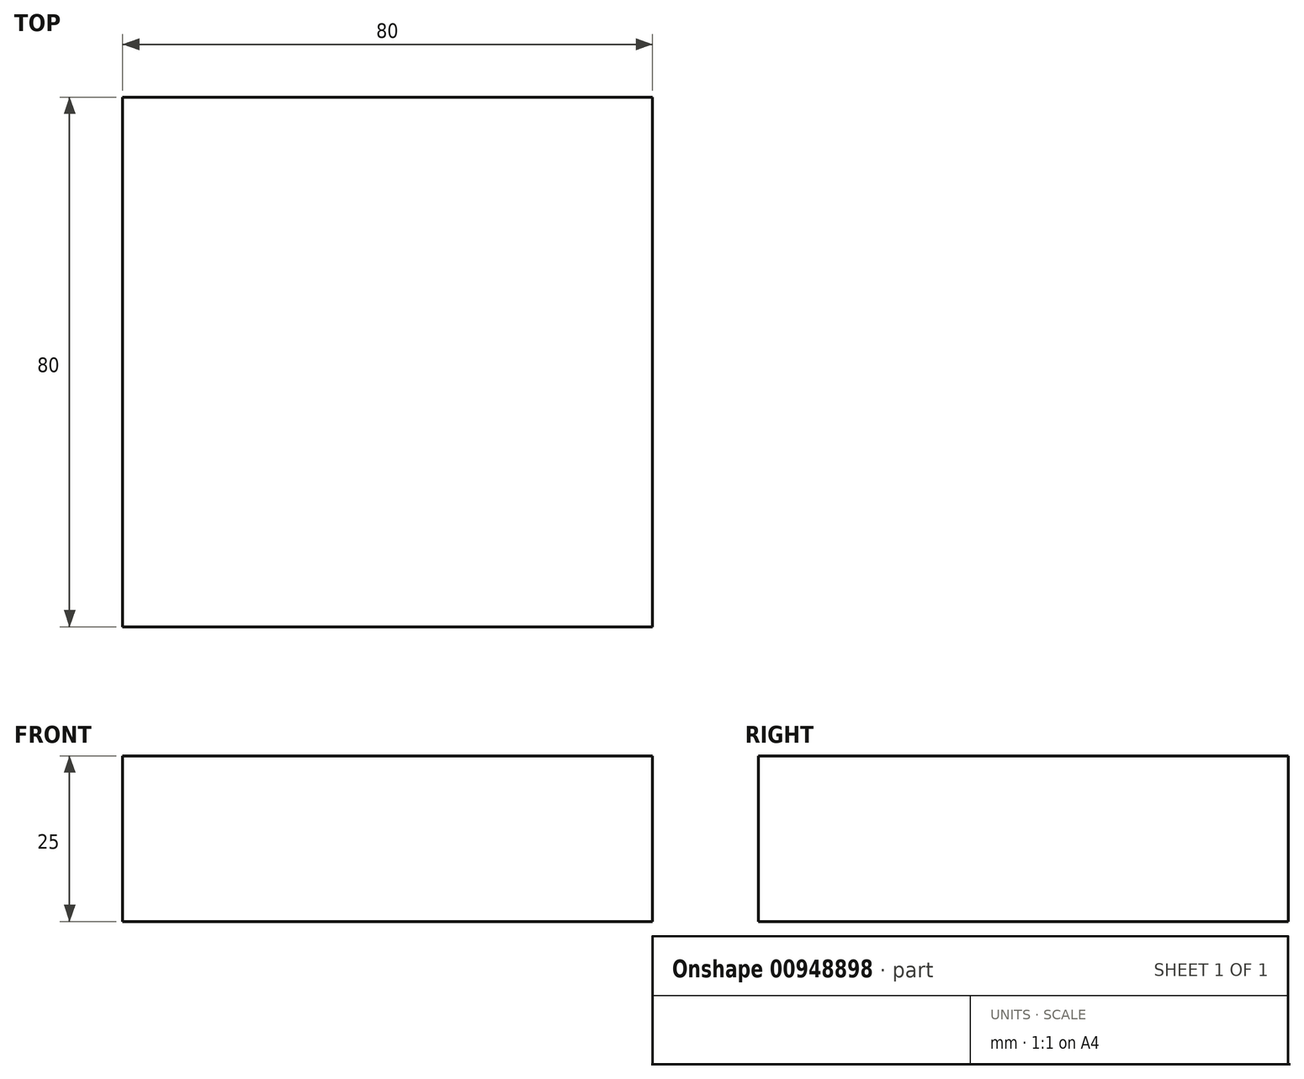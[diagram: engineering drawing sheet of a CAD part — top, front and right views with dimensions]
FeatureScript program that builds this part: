
annotation { "Feature Type Name" : "Feature", "Feature Type Description" : "" }
export const myFeature = defineFeature(function(context is Context, id is Id, definition is map)
    precondition{}
    {
        {
            var Q0;
            Q0=qCreatedBy(makeId("Top.planeOp"),FACE);
            var sketch = newSketch(context, id + "F0", { "sketchPlane" : qUnion([Q0])});
            skLineSegment(sketch, "E0.bottom", {"start": v(-52.06, 40.28) * mm, "end": v(27.94, 40.28) * mm});
            skLineSegment(sketch, "E0.top", {"start": v(-52.06, -39.72) * mm, "end": v(27.94, -39.72) * mm});
            skLineSegment(sketch, "E0.left", {"start": v(-52.06, 40.28) * mm, "end": v(-52.06, -39.72) * mm});
            skLineSegment(sketch, "E0.right", {"start": v(27.94, 40.28) * mm, "end": v(27.94, -39.72) * mm});
            skSolve(sketch);
        }
        {
            var Q0;
            Q0 = qSketchRegion(id + "F0", true);
            extrude(context, id + "F1", {"entities" : qUnion([Q0]), "depth" : 25 * mm, "offsetDistance" : 25 * mm});
        }
    });
